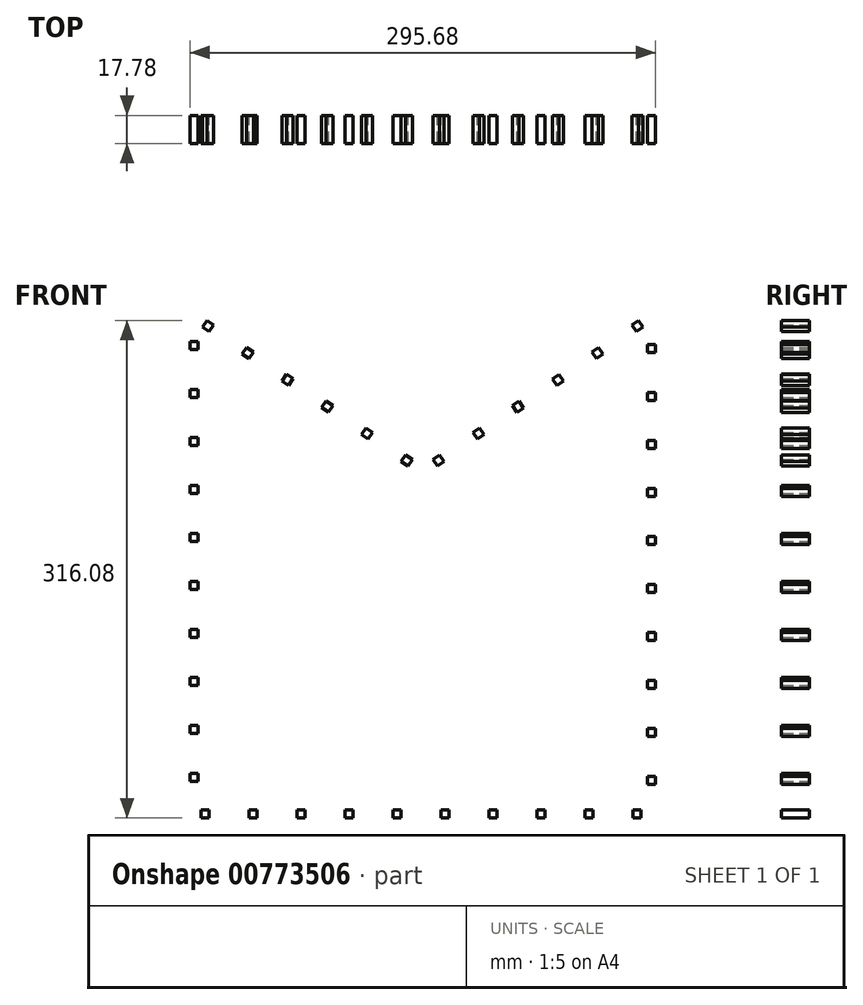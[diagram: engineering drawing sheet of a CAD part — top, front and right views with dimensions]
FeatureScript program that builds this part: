
annotation { "Feature Type Name" : "Feature", "Feature Type Description" : "" }
export const myFeature = defineFeature(function(context is Context, id is Id, definition is map)
    precondition{}
    {
        {
            var Q0;
            Q0=qCreatedBy(makeId("Front.planeOp"),FACE);
            var sketch = newSketch(context, id + "F0", { "sketchPlane" : qUnion([Q0])});
            skLineSegment(sketch, "E0", {"start": v(-10.13, 70.18) * mm, "end": v(-145.3, 161.55) * mm});
            skLineSegment(sketch, "E1", {"start": v(-145.3, 161.55) * mm, "end": v(-145.3, -154.49) * mm});
            skLineSegment(sketch, "E2", {"start": v(-145.3, -154.49) * mm, "end": v(145.3, -154.49) * mm});
            skLineSegment(sketch, "E3", {"start": v(145.3, -154.49) * mm, "end": v(145.3, 161.55) * mm});
            skLineSegment(sketch, "E4", {"start": v(145.3, 161.55) * mm, "end": v(10.13, 70.18) * mm});
            skPoint(sketch, "E5", {"position": v(0, 70.18) * mm});
            skPoint(sketch, "E6", {"position": v(0, -154.49) * mm});
            skSolve(sketch);
        }
        {
            var Q0;
            Q0=qCreatedBy(makeId("Front.planeOp"),FACE);
            var sketch = newSketch(context, id + "F1", { "sketchPlane" : qUnion([Q0])});
            skCircle(sketch, "E7.cCircle", {"center": v(-10.13, 70.18) * mm, "radius": 2.54 * mm, "construction": true});
            skLineSegment(sketch, "E7.0", {"start": v(-6.6, 70.86) * mm, "end": v(-9.44, 66.65) * mm});
            skLineSegment(sketch, "E7.1", {"start": v(-9.44, 66.65) * mm, "end": v(-13.65, 69.5) * mm});
            skLineSegment(sketch, "E7.2", {"start": v(-13.65, 69.5) * mm, "end": v(-10.8, 73.7) * mm});
            skLineSegment(sketch, "E7.3", {"start": v(-10.8, 73.7) * mm, "end": v(-6.6, 70.86) * mm});
            skPoint(sketch, "E7.0.midPoint", {"position": v(-8.02, 68.76) * mm});
            skCircle(sketch, "E8.cCircle", {"center": v(-35.38, 87.25) * mm, "radius": 2.54 * mm, "construction": true});
            skLineSegment(sketch, "E8.0", {"start": v(-31.85, 87.93) * mm, "end": v(-34.7, 83.72) * mm});
            skLineSegment(sketch, "E8.1", {"start": v(-34.7, 83.72) * mm, "end": v(-38.9, 86.57) * mm});
            skLineSegment(sketch, "E8.2", {"start": v(-38.9, 86.57) * mm, "end": v(-36.06, 90.77) * mm});
            skLineSegment(sketch, "E8.3", {"start": v(-36.06, 90.77) * mm, "end": v(-31.85, 87.93) * mm});
            skPoint(sketch, "E8.0.midPoint", {"position": v(-33.27, 85.82) * mm});
            skCircle(sketch, "E9.cCircle", {"center": v(-60.63, 104.32) * mm, "radius": 2.54 * mm, "construction": true});
            skLineSegment(sketch, "E9.0", {"start": v(-57.1, 105) * mm, "end": v(-59.95, 100.79) * mm});
            skLineSegment(sketch, "E9.1", {"start": v(-59.95, 100.79) * mm, "end": v(-64.16, 103.63) * mm});
            skLineSegment(sketch, "E9.2", {"start": v(-64.16, 103.63) * mm, "end": v(-61.31, 107.84) * mm});
            skLineSegment(sketch, "E9.3", {"start": v(-61.31, 107.84) * mm, "end": v(-57.1, 105) * mm});
            skPoint(sketch, "E9.0.midPoint", {"position": v(-58.53, 102.9) * mm});
            skCircle(sketch, "E10.cCircle", {"center": v(-85.88, 121.39) * mm, "radius": 2.54 * mm, "construction": true});
            skLineSegment(sketch, "E10.0", {"start": v(-82.36, 122.07) * mm, "end": v(-85.2, 117.86) * mm});
            skLineSegment(sketch, "E10.1", {"start": v(-85.2, 117.86) * mm, "end": v(-89.4, 120.7) * mm});
            skLineSegment(sketch, "E10.2", {"start": v(-89.4, 120.7) * mm, "end": v(-86.56, 124.91) * mm});
            skLineSegment(sketch, "E10.3", {"start": v(-86.56, 124.91) * mm, "end": v(-82.36, 122.07) * mm});
            skPoint(sketch, "E10.0.midPoint", {"position": v(-83.78, 119.96) * mm});
            skCircle(sketch, "E11.cCircle", {"center": v(-111.13, 138.46) * mm, "radius": 2.54 * mm, "construction": true});
            skLineSegment(sketch, "E11.0", {"start": v(-107.6, 139.14) * mm, "end": v(-110.45, 134.93) * mm});
            skLineSegment(sketch, "E11.1", {"start": v(-110.45, 134.93) * mm, "end": v(-114.66, 137.77) * mm});
            skLineSegment(sketch, "E11.2", {"start": v(-114.66, 137.77) * mm, "end": v(-111.82, 141.98) * mm});
            skLineSegment(sketch, "E11.3", {"start": v(-111.82, 141.98) * mm, "end": v(-107.6, 139.14) * mm});
            skPoint(sketch, "E11.0.midPoint", {"position": v(-109.03, 137.03) * mm});
            skCircle(sketch, "E12.cCircle", {"center": v(-136.39, 155.52) * mm, "radius": 2.54 * mm, "construction": true});
            skLineSegment(sketch, "E12.0", {"start": v(-132.86, 156.2) * mm, "end": v(-135.7, 152) * mm});
            skLineSegment(sketch, "E12.1", {"start": v(-135.7, 152) * mm, "end": v(-139.91, 154.84) * mm});
            skLineSegment(sketch, "E12.2", {"start": v(-139.91, 154.84) * mm, "end": v(-137.07, 159.05) * mm});
            skLineSegment(sketch, "E12.3", {"start": v(-137.07, 159.05) * mm, "end": v(-132.86, 156.2) * mm});
            skPoint(sketch, "E12.0.midPoint", {"position": v(-134.28, 154.1) * mm});
            skCircle(sketch, "E13.cCircle", {"center": v(-145.3, -9.4) * mm, "radius": 2.54 * mm, "construction": true});
            skLineSegment(sketch, "E13.0", {"start": v(-142.76, -11.93) * mm, "end": v(-147.84, -11.93) * mm});
            skLineSegment(sketch, "E13.1", {"start": v(-147.84, -11.93) * mm, "end": v(-147.84, -6.85) * mm});
            skLineSegment(sketch, "E13.2", {"start": v(-147.84, -6.85) * mm, "end": v(-142.76, -6.85) * mm});
            skLineSegment(sketch, "E13.3", {"start": v(-142.76, -6.85) * mm, "end": v(-142.76, -11.93) * mm});
            skPoint(sketch, "E13.0.midPoint", {"position": v(-145.3, -11.93) * mm});
            skCircle(sketch, "E14.cCircle", {"center": v(-145.3, 21.09) * mm, "radius": 2.54 * mm, "construction": true});
            skLineSegment(sketch, "E14.0", {"start": v(-142.76, 18.55) * mm, "end": v(-147.84, 18.55) * mm});
            skLineSegment(sketch, "E14.1", {"start": v(-147.84, 18.55) * mm, "end": v(-147.84, 23.63) * mm});
            skLineSegment(sketch, "E14.2", {"start": v(-147.84, 23.63) * mm, "end": v(-142.76, 23.63) * mm});
            skLineSegment(sketch, "E14.3", {"start": v(-142.76, 23.63) * mm, "end": v(-142.76, 18.55) * mm});
            skPoint(sketch, "E14.0.midPoint", {"position": v(-145.3, 18.55) * mm});
            skCircle(sketch, "E15.cCircle", {"center": v(-145.3, 51.57) * mm, "radius": 2.54 * mm, "construction": true});
            skLineSegment(sketch, "E15.0", {"start": v(-142.76, 49.03) * mm, "end": v(-147.84, 49.03) * mm});
            skLineSegment(sketch, "E15.1", {"start": v(-147.84, 49.03) * mm, "end": v(-147.84, 54.1) * mm});
            skLineSegment(sketch, "E15.2", {"start": v(-147.84, 54.1) * mm, "end": v(-142.76, 54.1) * mm});
            skLineSegment(sketch, "E15.3", {"start": v(-142.76, 54.1) * mm, "end": v(-142.76, 49.03) * mm});
            skPoint(sketch, "E15.0.midPoint", {"position": v(-145.3, 49.03) * mm});
            skCircle(sketch, "E16.cCircle", {"center": v(-145.3, 82.05) * mm, "radius": 2.54 * mm, "construction": true});
            skLineSegment(sketch, "E16.0", {"start": v(-142.76, 79.5) * mm, "end": v(-147.84, 79.5) * mm});
            skLineSegment(sketch, "E16.1", {"start": v(-147.84, 79.5) * mm, "end": v(-147.84, 84.59) * mm});
            skLineSegment(sketch, "E16.2", {"start": v(-147.84, 84.59) * mm, "end": v(-142.76, 84.59) * mm});
            skLineSegment(sketch, "E16.3", {"start": v(-142.76, 84.59) * mm, "end": v(-142.76, 79.5) * mm});
            skPoint(sketch, "E16.0.midPoint", {"position": v(-145.3, 79.5) * mm});
            skCircle(sketch, "E17.cCircle", {"center": v(-145.3, 112.53) * mm, "radius": 2.54 * mm, "construction": true});
            skLineSegment(sketch, "E17.0", {"start": v(-142.76, 109.99) * mm, "end": v(-147.84, 109.99) * mm});
            skLineSegment(sketch, "E17.1", {"start": v(-147.84, 109.99) * mm, "end": v(-147.84, 115.07) * mm});
            skLineSegment(sketch, "E17.2", {"start": v(-147.84, 115.07) * mm, "end": v(-142.76, 115.07) * mm});
            skLineSegment(sketch, "E17.3", {"start": v(-142.76, 115.07) * mm, "end": v(-142.76, 109.99) * mm});
            skPoint(sketch, "E17.0.midPoint", {"position": v(-145.3, 109.99) * mm});
            skCircle(sketch, "E18.cCircle", {"center": v(-145.3, 143) * mm, "radius": 2.54 * mm, "construction": true});
            skLineSegment(sketch, "E18.0", {"start": v(-142.76, 140.47) * mm, "end": v(-147.84, 140.47) * mm});
            skLineSegment(sketch, "E18.1", {"start": v(-147.84, 140.47) * mm, "end": v(-147.84, 145.55) * mm});
            skLineSegment(sketch, "E18.2", {"start": v(-147.84, 145.55) * mm, "end": v(-142.76, 145.55) * mm});
            skLineSegment(sketch, "E18.3", {"start": v(-142.76, 145.55) * mm, "end": v(-142.76, 140.47) * mm});
            skPoint(sketch, "E18.0.midPoint", {"position": v(-145.3, 140.47) * mm});
            skCircle(sketch, "E19.cCircle", {"center": v(-145.3, -131.31) * mm, "radius": 2.54 * mm, "construction": true});
            skLineSegment(sketch, "E19.0", {"start": v(-142.76, -133.85) * mm, "end": v(-147.84, -133.85) * mm});
            skLineSegment(sketch, "E19.1", {"start": v(-147.84, -133.85) * mm, "end": v(-147.84, -128.77) * mm});
            skLineSegment(sketch, "E19.2", {"start": v(-147.84, -128.77) * mm, "end": v(-142.76, -128.77) * mm});
            skLineSegment(sketch, "E19.3", {"start": v(-142.76, -128.77) * mm, "end": v(-142.76, -133.85) * mm});
            skPoint(sketch, "E19.0.midPoint", {"position": v(-145.3, -133.85) * mm});
            skCircle(sketch, "E20.cCircle", {"center": v(-145.3, -100.83) * mm, "radius": 2.54 * mm, "construction": true});
            skLineSegment(sketch, "E20.0", {"start": v(-142.76, -103.37) * mm, "end": v(-147.84, -103.37) * mm});
            skLineSegment(sketch, "E20.1", {"start": v(-147.84, -103.37) * mm, "end": v(-147.84, -98.3) * mm});
            skLineSegment(sketch, "E20.2", {"start": v(-147.84, -98.3) * mm, "end": v(-142.76, -98.3) * mm});
            skLineSegment(sketch, "E20.3", {"start": v(-142.76, -98.3) * mm, "end": v(-142.76, -103.37) * mm});
            skPoint(sketch, "E20.0.midPoint", {"position": v(-145.3, -103.37) * mm});
            skCircle(sketch, "E21.cCircle", {"center": v(-145.3, -70.35) * mm, "radius": 2.54 * mm, "construction": true});
            skLineSegment(sketch, "E21.0", {"start": v(-142.76, -72.9) * mm, "end": v(-147.84, -72.9) * mm});
            skLineSegment(sketch, "E21.1", {"start": v(-147.84, -72.9) * mm, "end": v(-147.84, -67.81) * mm});
            skLineSegment(sketch, "E21.2", {"start": v(-147.84, -67.81) * mm, "end": v(-142.76, -67.81) * mm});
            skLineSegment(sketch, "E21.3", {"start": v(-142.76, -67.81) * mm, "end": v(-142.76, -72.9) * mm});
            skPoint(sketch, "E21.0.midPoint", {"position": v(-145.3, -72.9) * mm});
            skCircle(sketch, "E22.cCircle", {"center": v(-145.3, -39.87) * mm, "radius": 2.54 * mm, "construction": true});
            skLineSegment(sketch, "E22.0", {"start": v(-142.76, -42.41) * mm, "end": v(-147.84, -42.41) * mm});
            skLineSegment(sketch, "E22.1", {"start": v(-147.84, -42.41) * mm, "end": v(-147.84, -37.33) * mm});
            skLineSegment(sketch, "E22.2", {"start": v(-147.84, -37.33) * mm, "end": v(-142.76, -37.33) * mm});
            skLineSegment(sketch, "E22.3", {"start": v(-142.76, -37.33) * mm, "end": v(-142.76, -42.41) * mm});
            skPoint(sketch, "E22.0.midPoint", {"position": v(-145.3, -42.41) * mm});
            skCircle(sketch, "E23.cCircle", {"center": v(-16.27, -154.49) * mm, "radius": 2.54 * mm, "construction": true});
            skLineSegment(sketch, "E23.0", {"start": v(-18.8, -157.03) * mm, "end": v(-18.8, -151.95) * mm});
            skLineSegment(sketch, "E23.1", {"start": v(-18.8, -151.95) * mm, "end": v(-13.73, -151.95) * mm});
            skLineSegment(sketch, "E23.2", {"start": v(-13.73, -151.95) * mm, "end": v(-13.73, -157.03) * mm});
            skLineSegment(sketch, "E23.3", {"start": v(-13.73, -157.03) * mm, "end": v(-18.8, -157.03) * mm});
            skPoint(sketch, "E23.0.midPoint", {"position": v(-18.8, -154.49) * mm});
            skCircle(sketch, "E24.cCircle", {"center": v(14.21, -154.49) * mm, "radius": 2.54 * mm, "construction": true});
            skLineSegment(sketch, "E24.0", {"start": v(11.67, -157.03) * mm, "end": v(11.67, -151.95) * mm});
            skLineSegment(sketch, "E24.1", {"start": v(11.67, -151.95) * mm, "end": v(16.75, -151.95) * mm});
            skLineSegment(sketch, "E24.2", {"start": v(16.75, -151.95) * mm, "end": v(16.75, -157.03) * mm});
            skLineSegment(sketch, "E24.3", {"start": v(16.75, -157.03) * mm, "end": v(11.67, -157.03) * mm});
            skPoint(sketch, "E24.0.midPoint", {"position": v(11.67, -154.49) * mm});
            skCircle(sketch, "E25.cCircle", {"center": v(44.7, -154.49) * mm, "radius": 2.54 * mm, "construction": true});
            skLineSegment(sketch, "E25.0", {"start": v(42.15, -157.03) * mm, "end": v(42.15, -151.95) * mm});
            skLineSegment(sketch, "E25.1", {"start": v(42.15, -151.95) * mm, "end": v(47.23, -151.95) * mm});
            skLineSegment(sketch, "E25.2", {"start": v(47.23, -151.95) * mm, "end": v(47.23, -157.03) * mm});
            skLineSegment(sketch, "E25.3", {"start": v(47.23, -157.03) * mm, "end": v(42.15, -157.03) * mm});
            skPoint(sketch, "E25.0.midPoint", {"position": v(42.15, -154.49) * mm});
            skCircle(sketch, "E26.cCircle", {"center": v(75.17, -154.49) * mm, "radius": 2.54 * mm, "construction": true});
            skLineSegment(sketch, "E26.0", {"start": v(72.63, -157.03) * mm, "end": v(72.63, -151.95) * mm});
            skLineSegment(sketch, "E26.1", {"start": v(72.63, -151.95) * mm, "end": v(77.71, -151.95) * mm});
            skLineSegment(sketch, "E26.2", {"start": v(77.71, -151.95) * mm, "end": v(77.71, -157.03) * mm});
            skLineSegment(sketch, "E26.3", {"start": v(77.71, -157.03) * mm, "end": v(72.63, -157.03) * mm});
            skPoint(sketch, "E26.0.midPoint", {"position": v(72.63, -154.49) * mm});
            skCircle(sketch, "E27.cCircle", {"center": v(105.65, -154.49) * mm, "radius": 2.54 * mm, "construction": true});
            skLineSegment(sketch, "E27.0", {"start": v(103.11, -157.03) * mm, "end": v(103.11, -151.95) * mm});
            skLineSegment(sketch, "E27.1", {"start": v(103.11, -151.95) * mm, "end": v(108.2, -151.95) * mm});
            skLineSegment(sketch, "E27.2", {"start": v(108.2, -151.95) * mm, "end": v(108.2, -157.03) * mm});
            skLineSegment(sketch, "E27.3", {"start": v(108.2, -157.03) * mm, "end": v(103.11, -157.03) * mm});
            skPoint(sketch, "E27.0.midPoint", {"position": v(103.11, -154.49) * mm});
            skCircle(sketch, "E28.cCircle", {"center": v(-138.19, -154.49) * mm, "radius": 2.54 * mm, "construction": true});
            skLineSegment(sketch, "E28.0", {"start": v(-140.73, -157.03) * mm, "end": v(-140.73, -151.95) * mm});
            skLineSegment(sketch, "E28.1", {"start": v(-140.73, -151.95) * mm, "end": v(-135.65, -151.95) * mm});
            skLineSegment(sketch, "E28.2", {"start": v(-135.65, -151.95) * mm, "end": v(-135.65, -157.03) * mm});
            skLineSegment(sketch, "E28.3", {"start": v(-135.65, -157.03) * mm, "end": v(-140.73, -157.03) * mm});
            skPoint(sketch, "E28.0.midPoint", {"position": v(-140.73, -154.49) * mm});
            skCircle(sketch, "E29.cCircle", {"center": v(-107.7, -154.49) * mm, "radius": 2.54 * mm, "construction": true});
            skLineSegment(sketch, "E29.0", {"start": v(-110.25, -157.03) * mm, "end": v(-110.25, -151.95) * mm});
            skLineSegment(sketch, "E29.1", {"start": v(-110.25, -151.95) * mm, "end": v(-105.17, -151.95) * mm});
            skLineSegment(sketch, "E29.2", {"start": v(-105.17, -151.95) * mm, "end": v(-105.17, -157.03) * mm});
            skLineSegment(sketch, "E29.3", {"start": v(-105.17, -157.03) * mm, "end": v(-110.25, -157.03) * mm});
            skPoint(sketch, "E29.0.midPoint", {"position": v(-110.25, -154.49) * mm});
            skCircle(sketch, "E30.cCircle", {"center": v(-77.23, -154.49) * mm, "radius": 2.54 * mm, "construction": true});
            skLineSegment(sketch, "E30.0", {"start": v(-79.77, -157.03) * mm, "end": v(-79.77, -151.95) * mm});
            skLineSegment(sketch, "E30.1", {"start": v(-79.77, -151.95) * mm, "end": v(-74.69, -151.95) * mm});
            skLineSegment(sketch, "E30.2", {"start": v(-74.69, -151.95) * mm, "end": v(-74.69, -157.03) * mm});
            skLineSegment(sketch, "E30.3", {"start": v(-74.69, -157.03) * mm, "end": v(-79.77, -157.03) * mm});
            skPoint(sketch, "E30.0.midPoint", {"position": v(-79.77, -154.49) * mm});
            skCircle(sketch, "E31.cCircle", {"center": v(-46.75, -154.49) * mm, "radius": 2.54 * mm, "construction": true});
            skLineSegment(sketch, "E31.0", {"start": v(-49.29, -157.03) * mm, "end": v(-49.29, -151.95) * mm});
            skLineSegment(sketch, "E31.1", {"start": v(-49.29, -151.95) * mm, "end": v(-44.2, -151.95) * mm});
            skLineSegment(sketch, "E31.2", {"start": v(-44.2, -151.95) * mm, "end": v(-44.2, -157.03) * mm});
            skLineSegment(sketch, "E31.3", {"start": v(-44.2, -157.03) * mm, "end": v(-49.29, -157.03) * mm});
            skPoint(sketch, "E31.0.midPoint", {"position": v(-49.29, -154.49) * mm});
            skCircle(sketch, "E32.cCircle", {"center": v(136.13, -154.49) * mm, "radius": 2.54 * mm, "construction": true});
            skLineSegment(sketch, "E32.0", {"start": v(133.6, -157.03) * mm, "end": v(133.6, -151.95) * mm});
            skLineSegment(sketch, "E32.1", {"start": v(133.6, -151.95) * mm, "end": v(138.67, -151.95) * mm});
            skLineSegment(sketch, "E32.2", {"start": v(138.67, -151.95) * mm, "end": v(138.67, -157.03) * mm});
            skLineSegment(sketch, "E32.3", {"start": v(138.67, -157.03) * mm, "end": v(133.6, -157.03) * mm});
            skPoint(sketch, "E32.0.midPoint", {"position": v(133.6, -154.49) * mm});
            skCircle(sketch, "E33.cCircle", {"center": v(145.3, -11.23) * mm, "radius": 2.54 * mm, "construction": true});
            skLineSegment(sketch, "E33.0", {"start": v(147.84, -13.77) * mm, "end": v(142.76, -13.77) * mm});
            skLineSegment(sketch, "E33.1", {"start": v(142.76, -13.77) * mm, "end": v(142.76, -8.69) * mm});
            skLineSegment(sketch, "E33.2", {"start": v(142.76, -8.69) * mm, "end": v(147.84, -8.69) * mm});
            skLineSegment(sketch, "E33.3", {"start": v(147.84, -8.69) * mm, "end": v(147.84, -13.77) * mm});
            skPoint(sketch, "E33.0.midPoint", {"position": v(145.3, -13.77) * mm});
            skCircle(sketch, "E34.cCircle", {"center": v(145.3, 19.25) * mm, "radius": 2.54 * mm, "construction": true});
            skLineSegment(sketch, "E34.0", {"start": v(147.84, 16.71) * mm, "end": v(142.76, 16.71) * mm});
            skLineSegment(sketch, "E34.1", {"start": v(142.76, 16.71) * mm, "end": v(142.76, 21.8) * mm});
            skLineSegment(sketch, "E34.2", {"start": v(142.76, 21.8) * mm, "end": v(147.84, 21.8) * mm});
            skLineSegment(sketch, "E34.3", {"start": v(147.84, 21.8) * mm, "end": v(147.84, 16.71) * mm});
            skPoint(sketch, "E34.0.midPoint", {"position": v(145.3, 16.71) * mm});
            skCircle(sketch, "E35.cCircle", {"center": v(145.3, 49.73) * mm, "radius": 2.54 * mm, "construction": true});
            skLineSegment(sketch, "E35.0", {"start": v(147.84, 47.2) * mm, "end": v(142.76, 47.2) * mm});
            skLineSegment(sketch, "E35.1", {"start": v(142.76, 47.2) * mm, "end": v(142.76, 52.27) * mm});
            skLineSegment(sketch, "E35.2", {"start": v(142.76, 52.27) * mm, "end": v(147.84, 52.27) * mm});
            skLineSegment(sketch, "E35.3", {"start": v(147.84, 52.27) * mm, "end": v(147.84, 47.2) * mm});
            skPoint(sketch, "E35.0.midPoint", {"position": v(145.3, 47.2) * mm});
            skCircle(sketch, "E36.cCircle", {"center": v(145.3, 80.21) * mm, "radius": 2.54 * mm, "construction": true});
            skLineSegment(sketch, "E36.0", {"start": v(147.84, 77.67) * mm, "end": v(142.76, 77.67) * mm});
            skLineSegment(sketch, "E36.1", {"start": v(142.76, 77.67) * mm, "end": v(142.76, 82.75) * mm});
            skLineSegment(sketch, "E36.2", {"start": v(142.76, 82.75) * mm, "end": v(147.84, 82.75) * mm});
            skLineSegment(sketch, "E36.3", {"start": v(147.84, 82.75) * mm, "end": v(147.84, 77.67) * mm});
            skPoint(sketch, "E36.0.midPoint", {"position": v(145.3, 77.67) * mm});
            skCircle(sketch, "E37.cCircle", {"center": v(145.3, 110.7) * mm, "radius": 2.54 * mm, "construction": true});
            skLineSegment(sketch, "E37.0", {"start": v(147.84, 108.15) * mm, "end": v(142.76, 108.15) * mm});
            skLineSegment(sketch, "E37.1", {"start": v(142.76, 108.15) * mm, "end": v(142.76, 113.23) * mm});
            skLineSegment(sketch, "E37.2", {"start": v(142.76, 113.23) * mm, "end": v(147.84, 113.23) * mm});
            skLineSegment(sketch, "E37.3", {"start": v(147.84, 113.23) * mm, "end": v(147.84, 108.15) * mm});
            skPoint(sketch, "E37.0.midPoint", {"position": v(145.3, 108.15) * mm});
            skCircle(sketch, "E38.cCircle", {"center": v(145.3, 141.17) * mm, "radius": 2.54 * mm, "construction": true});
            skLineSegment(sketch, "E38.0", {"start": v(147.84, 138.63) * mm, "end": v(142.76, 138.63) * mm});
            skLineSegment(sketch, "E38.1", {"start": v(142.76, 138.63) * mm, "end": v(142.76, 143.71) * mm});
            skLineSegment(sketch, "E38.2", {"start": v(142.76, 143.71) * mm, "end": v(147.84, 143.71) * mm});
            skLineSegment(sketch, "E38.3", {"start": v(147.84, 143.71) * mm, "end": v(147.84, 138.63) * mm});
            skPoint(sketch, "E38.0.midPoint", {"position": v(145.3, 138.63) * mm});
            skCircle(sketch, "E39.cCircle", {"center": v(145.3, -133.15) * mm, "radius": 2.54 * mm, "construction": true});
            skLineSegment(sketch, "E39.0", {"start": v(147.84, -135.69) * mm, "end": v(142.76, -135.69) * mm});
            skLineSegment(sketch, "E39.1", {"start": v(142.76, -135.69) * mm, "end": v(142.76, -130.6) * mm});
            skLineSegment(sketch, "E39.2", {"start": v(142.76, -130.6) * mm, "end": v(147.84, -130.6) * mm});
            skLineSegment(sketch, "E39.3", {"start": v(147.84, -130.6) * mm, "end": v(147.84, -135.69) * mm});
            skPoint(sketch, "E39.0.midPoint", {"position": v(145.3, -135.69) * mm});
            skCircle(sketch, "E40.cCircle", {"center": v(145.3, -102.67) * mm, "radius": 2.54 * mm, "construction": true});
            skLineSegment(sketch, "E40.0", {"start": v(147.84, -105.2) * mm, "end": v(142.76, -105.2) * mm});
            skLineSegment(sketch, "E40.1", {"start": v(142.76, -105.2) * mm, "end": v(142.76, -100.13) * mm});
            skLineSegment(sketch, "E40.2", {"start": v(142.76, -100.13) * mm, "end": v(147.84, -100.13) * mm});
            skLineSegment(sketch, "E40.3", {"start": v(147.84, -100.13) * mm, "end": v(147.84, -105.2) * mm});
            skPoint(sketch, "E40.0.midPoint", {"position": v(145.3, -105.2) * mm});
            skCircle(sketch, "E41.cCircle", {"center": v(145.3, -72.19) * mm, "radius": 2.54 * mm, "construction": true});
            skLineSegment(sketch, "E41.0", {"start": v(147.84, -74.73) * mm, "end": v(142.76, -74.73) * mm});
            skLineSegment(sketch, "E41.1", {"start": v(142.76, -74.73) * mm, "end": v(142.76, -69.65) * mm});
            skLineSegment(sketch, "E41.2", {"start": v(142.76, -69.65) * mm, "end": v(147.84, -69.65) * mm});
            skLineSegment(sketch, "E41.3", {"start": v(147.84, -69.65) * mm, "end": v(147.84, -74.73) * mm});
            skPoint(sketch, "E41.0.midPoint", {"position": v(145.3, -74.73) * mm});
            skCircle(sketch, "E42.cCircle", {"center": v(145.3, -41.7) * mm, "radius": 2.54 * mm, "construction": true});
            skLineSegment(sketch, "E42.0", {"start": v(147.84, -44.25) * mm, "end": v(142.76, -44.25) * mm});
            skLineSegment(sketch, "E42.1", {"start": v(142.76, -44.25) * mm, "end": v(142.76, -39.17) * mm});
            skLineSegment(sketch, "E42.2", {"start": v(142.76, -39.17) * mm, "end": v(147.84, -39.17) * mm});
            skLineSegment(sketch, "E42.3", {"start": v(147.84, -39.17) * mm, "end": v(147.84, -44.25) * mm});
            skPoint(sketch, "E42.0.midPoint", {"position": v(145.3, -44.25) * mm});
            skCircle(sketch, "E43.cCircle", {"center": v(10.08, 70.14) * mm, "radius": 2.54 * mm, "construction": true});
            skLineSegment(sketch, "E43.0", {"start": v(9.4, 66.62) * mm, "end": v(6.55, 70.83) * mm});
            skLineSegment(sketch, "E43.1", {"start": v(6.55, 70.83) * mm, "end": v(10.76, 73.67) * mm});
            skLineSegment(sketch, "E43.2", {"start": v(10.76, 73.67) * mm, "end": v(13.6, 69.46) * mm});
            skLineSegment(sketch, "E43.3", {"start": v(13.6, 69.46) * mm, "end": v(9.4, 66.62) * mm});
            skPoint(sketch, "E43.0.midPoint", {"position": v(7.97, 68.72) * mm});
            skCircle(sketch, "E44.cCircle", {"center": v(35.33, 87.21) * mm, "radius": 2.54 * mm, "construction": true});
            skLineSegment(sketch, "E44.0", {"start": v(34.65, 83.69) * mm, "end": v(31.8, 87.9) * mm});
            skLineSegment(sketch, "E44.1", {"start": v(31.8, 87.9) * mm, "end": v(36.01, 90.74) * mm});
            skLineSegment(sketch, "E44.2", {"start": v(36.01, 90.74) * mm, "end": v(38.86, 86.53) * mm});
            skLineSegment(sketch, "E44.3", {"start": v(38.86, 86.53) * mm, "end": v(34.65, 83.69) * mm});
            skPoint(sketch, "E44.0.midPoint", {"position": v(33.22, 85.8) * mm});
            skCircle(sketch, "E45.cCircle", {"center": v(60.58, 104.28) * mm, "radius": 2.54 * mm, "construction": true});
            skLineSegment(sketch, "E45.0", {"start": v(59.9, 100.76) * mm, "end": v(57.05, 104.96) * mm});
            skLineSegment(sketch, "E45.1", {"start": v(57.05, 104.96) * mm, "end": v(61.26, 107.8) * mm});
            skLineSegment(sketch, "E45.2", {"start": v(61.26, 107.8) * mm, "end": v(64.1, 103.6) * mm});
            skLineSegment(sketch, "E45.3", {"start": v(64.1, 103.6) * mm, "end": v(59.9, 100.76) * mm});
            skPoint(sketch, "E45.0.midPoint", {"position": v(58.48, 102.86) * mm});
            skCircle(sketch, "E46.cCircle", {"center": v(85.83, 121.35) * mm, "radius": 2.54 * mm, "construction": true});
            skLineSegment(sketch, "E46.0", {"start": v(85.15, 117.83) * mm, "end": v(82.3, 122.03) * mm});
            skLineSegment(sketch, "E46.1", {"start": v(82.3, 122.03) * mm, "end": v(86.51, 124.88) * mm});
            skLineSegment(sketch, "E46.2", {"start": v(86.51, 124.88) * mm, "end": v(89.36, 120.67) * mm});
            skLineSegment(sketch, "E46.3", {"start": v(89.36, 120.67) * mm, "end": v(85.15, 117.83) * mm});
            skPoint(sketch, "E46.0.midPoint", {"position": v(83.73, 119.93) * mm});
            skCircle(sketch, "E47.cCircle", {"center": v(111.08, 138.42) * mm, "radius": 2.54 * mm, "construction": true});
            skLineSegment(sketch, "E47.0", {"start": v(110.4, 134.9) * mm, "end": v(107.56, 139.1) * mm});
            skLineSegment(sketch, "E47.1", {"start": v(107.56, 139.1) * mm, "end": v(111.77, 141.95) * mm});
            skLineSegment(sketch, "E47.2", {"start": v(111.77, 141.95) * mm, "end": v(114.61, 137.74) * mm});
            skLineSegment(sketch, "E47.3", {"start": v(114.61, 137.74) * mm, "end": v(110.4, 134.9) * mm});
            skPoint(sketch, "E47.0.midPoint", {"position": v(108.98, 137) * mm});
            skCircle(sketch, "E48.cCircle", {"center": v(136.34, 155.5) * mm, "radius": 2.54 * mm, "construction": true});
            skLineSegment(sketch, "E48.0", {"start": v(135.65, 151.96) * mm, "end": v(132.8, 156.17) * mm});
            skLineSegment(sketch, "E48.1", {"start": v(132.8, 156.17) * mm, "end": v(137.02, 159.02) * mm});
            skLineSegment(sketch, "E48.2", {"start": v(137.02, 159.02) * mm, "end": v(139.86, 154.8) * mm});
            skLineSegment(sketch, "E48.3", {"start": v(139.86, 154.8) * mm, "end": v(135.65, 151.96) * mm});
            skPoint(sketch, "E48.0.midPoint", {"position": v(134.23, 154.07) * mm});
            skSolve(sketch);
        }
        {
            var Q0;
            Q0 = qSketchRegion(id + "F1", true);
            extrude(context, id + "F2", {"entities" : qUnion([Q0]), "depth" : 17.78 * mm, "offsetDistance" : 25.4 * mm});
        }
    });
